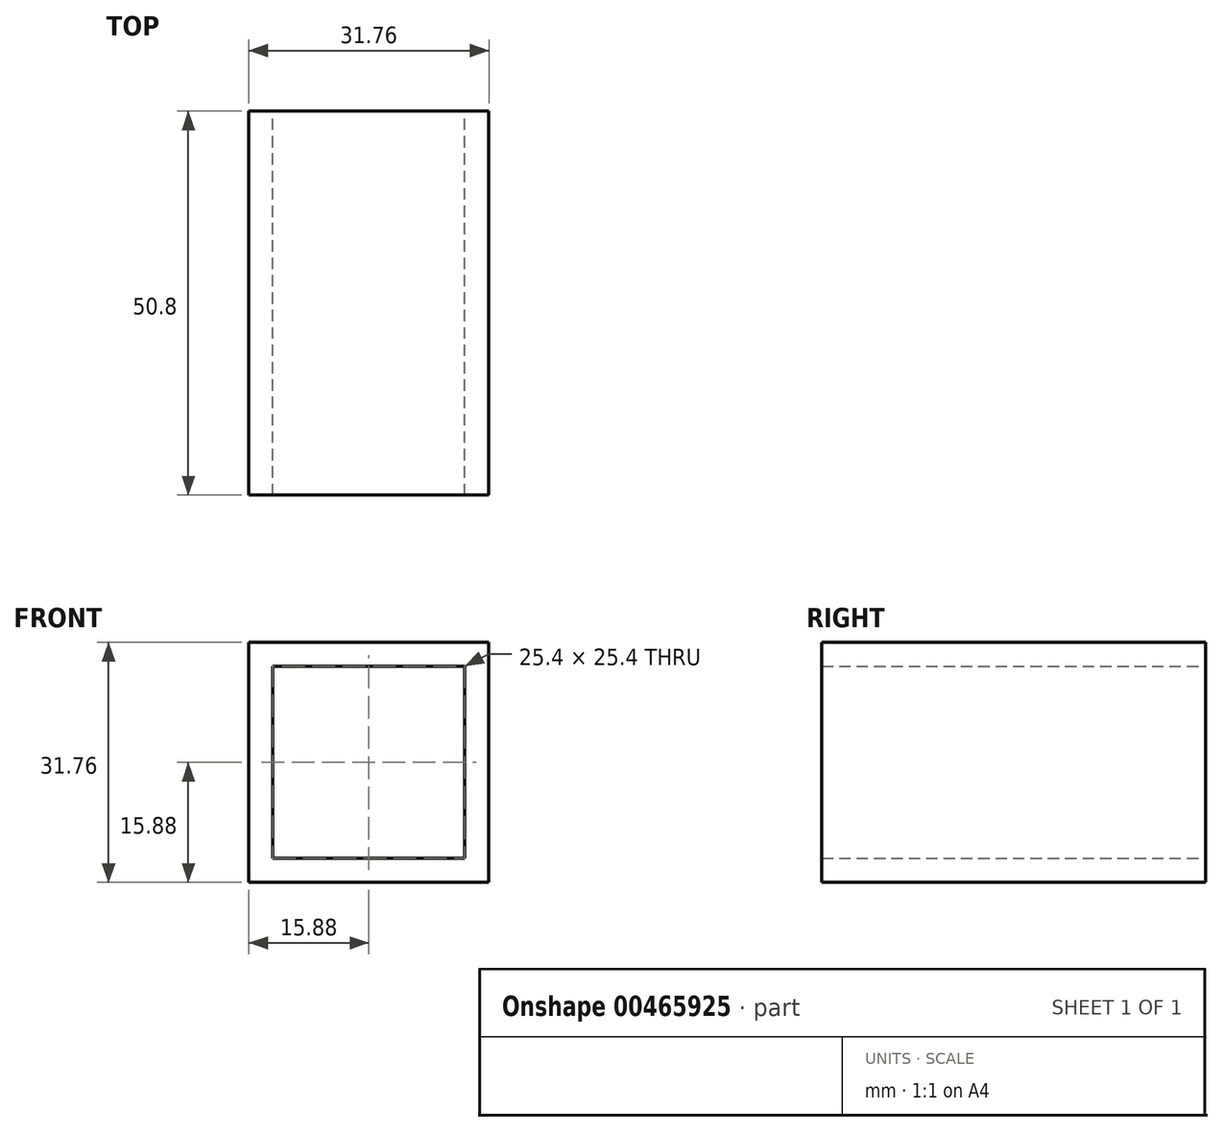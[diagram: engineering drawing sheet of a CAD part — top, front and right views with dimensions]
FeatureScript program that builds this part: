
annotation { "Feature Type Name" : "Feature", "Feature Type Description" : "" }
export const myFeature = defineFeature(function(context is Context, id is Id, definition is map)
    precondition{}
    {
        {
            var Q0;
            Q0=qCreatedBy(makeId("Front.planeOp"),FACE);
            var sketch = newSketch(context, id + "F0", { "sketchPlane" : qUnion([Q0])});
            skLineSegment(sketch, "E0.bottom", {"start": v(-15.87, 15.88) * mm, "end": v(15.88, 15.88) * mm});
            skLineSegment(sketch, "E0.top", {"start": v(-15.88, -15.88) * mm, "end": v(15.87, -15.88) * mm});
            skLineSegment(sketch, "E0.left", {"start": v(-15.87, 15.88) * mm, "end": v(-15.88, -15.88) * mm});
            skLineSegment(sketch, "E0.right", {"start": v(15.88, 15.88) * mm, "end": v(15.87, -15.88) * mm});
            skPoint(sketch, "E0.middle", {"position": v(0, 0) * mm});
            skLineSegment(sketch, "E1.bottom", {"start": v(-12.7, 12.7) * mm, "end": v(12.7, 12.7) * mm});
            skLineSegment(sketch, "E1.top", {"start": v(-12.7, -12.7) * mm, "end": v(12.7, -12.7) * mm});
            skLineSegment(sketch, "E1.left", {"start": v(-12.7, 12.7) * mm, "end": v(-12.7, -12.7) * mm});
            skLineSegment(sketch, "E1.right", {"start": v(12.7, 12.7) * mm, "end": v(12.7, -12.7) * mm});
            skSolve(sketch);
        }
        {
            var Q0;
            Q0=makeQuery(id+"F0.imprint","IMPRINT",FACE,{"disambiguationData":[TD([[makeQuery(id+"F0.imprint","IMPRINT",EDGE,{"derivedFrom":sQuery(id+"F0.wireOp",EDGE,"E0.bottom")}),-1.0]])]});
            extrude(context, id + "F1", {"entities" : qUnion([Q0]), "endBound" : BoundingType.SYMMETRIC, "depth" : 50.8 * mm});
        }
    });
